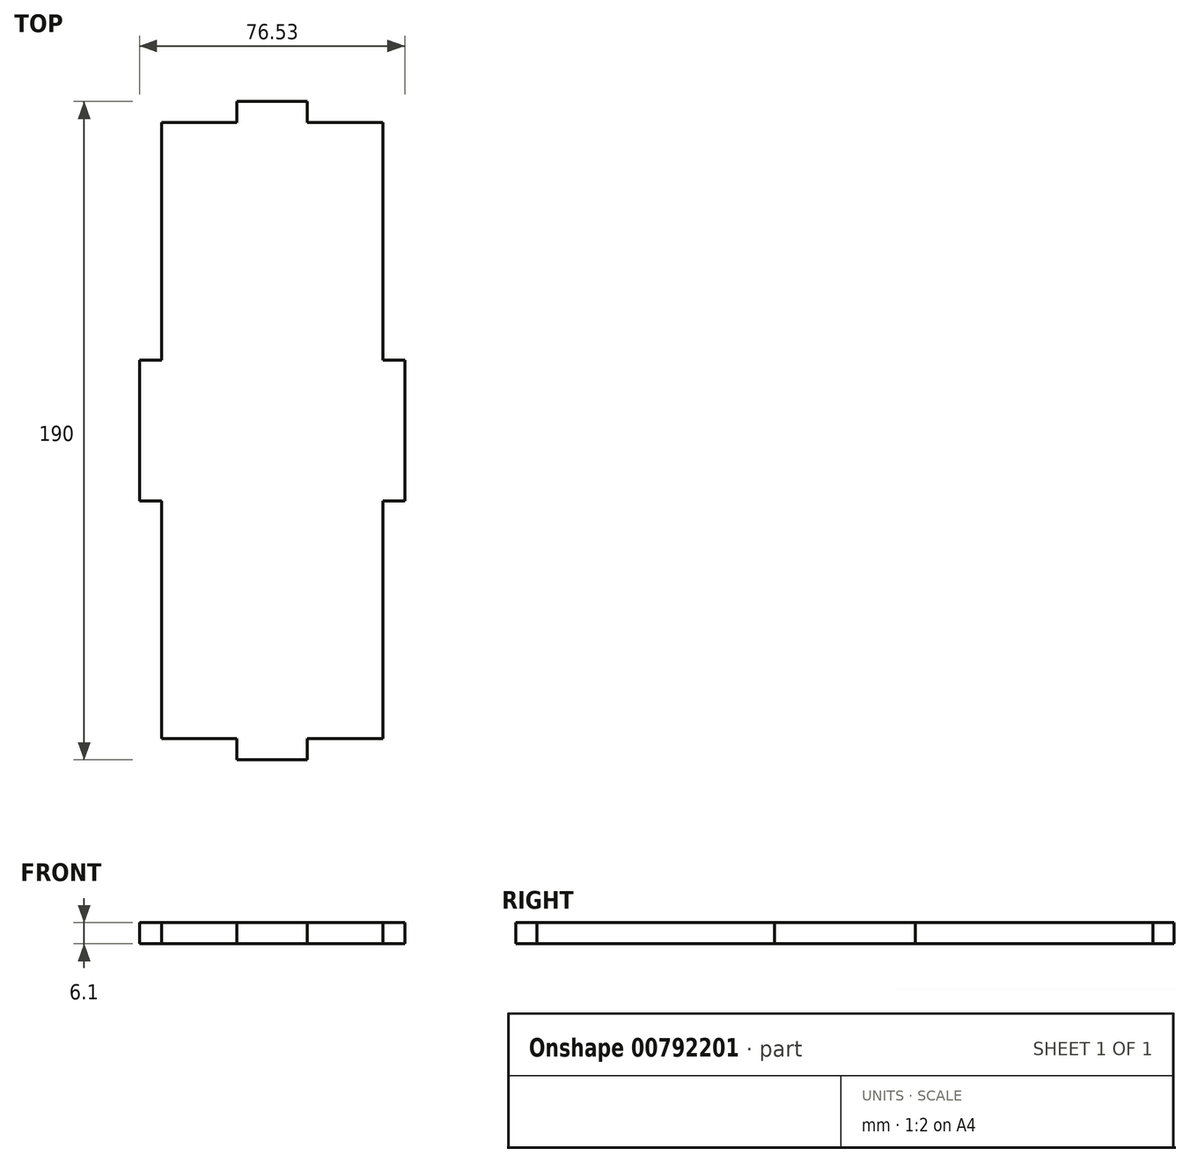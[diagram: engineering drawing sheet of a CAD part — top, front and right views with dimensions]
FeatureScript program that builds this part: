
annotation { "Feature Type Name" : "Feature", "Feature Type Description" : "" }
export const myFeature = defineFeature(function(context is Context, id is Id, definition is map)
    precondition{}
    {
        {
            var Q0;
            Q0=qCreatedBy(makeId("Top.planeOp"),FACE);
            var sketch = newSketch(context, id + "F0", { "sketchPlane" : qUnion([Q0])});
            skLineSegment(sketch, "E0.top", {"start": v(-37.7, 23.44) * mm, "end": v(-31.36, 23.44) * mm});
            skLineSegment(sketch, "E1.MirrorCS", {"start": v(-37.7, -17.2) * mm, "end": v(-31.36, -17.2) * mm});
            skLineSegment(sketch, "E2.MirrorCS", {"start": v(38.82, 23.44) * mm, "end": v(32.47, 23.44) * mm});
            skLineSegment(sketch, "E3.MirrorCS", {"start": v(38.82, -17.2) * mm, "end": v(32.47, -17.2) * mm});
            skLineSegment(sketch, "E4", {"start": v(-37.7, -17.2) * mm, "end": v(-37.7, 23.44) * mm});
            skLineSegment(sketch, "E5", {"start": v(38.82, -17.2) * mm, "end": v(38.82, 23.44) * mm});
            skLineSegment(sketch, "E6", {"start": v(-31.36, -17.2) * mm, "end": v(-31.36, -85.78) * mm});
            skLineSegment(sketch, "E7", {"start": v(32.47, -17.2) * mm, "end": v(32.47, -85.78) * mm});
            skLineSegment(sketch, "E8", {"start": v(-31.36, 23.44) * mm, "end": v(-31.36, 92.02) * mm});
            skLineSegment(sketch, "E9", {"start": v(32.47, 23.44) * mm, "end": v(32.47, 92.02) * mm});
            skLineSegment(sketch, "E10", {"start": v(-31.36, -85.78) * mm, "end": v(-9.6, -85.78) * mm});
            skLineSegment(sketch, "E11", {"start": v(32.47, 92.02) * mm, "end": v(10.71, 92.02) * mm});
            skLineSegment(sketch, "E12", {"start": v(32.47, -85.78) * mm, "end": v(10.71, -85.78) * mm});
            skLineSegment(sketch, "E13", {"start": v(10.71, -85.78) * mm, "end": v(10.71, -91.88) * mm});
            skLineSegment(sketch, "E14", {"start": v(10.71, -91.88) * mm, "end": v(-9.6, -91.88) * mm});
            skLineSegment(sketch, "E15", {"start": v(-9.6, -91.88) * mm, "end": v(-9.6, -85.78) * mm});
            skPoint(sketch, "E16.orphan", {"position": v(0.55, -85.78) * mm});
            skLineSegment(sketch, "E17.MirrorCS", {"start": v(-9.6, 98.12) * mm, "end": v(-9.6, 92.02) * mm});
            skLineSegment(sketch, "E18.MirrorCS", {"start": v(10.71, 98.12) * mm, "end": v(-9.6, 98.12) * mm});
            skLineSegment(sketch, "E19.MirrorCS", {"start": v(10.71, 92.02) * mm, "end": v(10.71, 98.12) * mm});
            skPoint(sketch, "E20.end.orphan", {"position": v(38.82, 3.12) * mm});
            skPoint(sketch, "E20.start.orphan", {"position": v(-37.7, 3.12) * mm});
            skLineSegment(sketch, "E21.trimOffspring", {"start": v(-9.6, 92.02) * mm, "end": v(-31.36, 92.02) * mm});
            skSolve(sketch);
        }
        {
            var Q0;
            Q0=makeQuery(id+"F0.imprint","IMPRINT",FACE,{"disambiguationData":[TD([[makeQuery(id+"F0.imprint","IMPRINT",EDGE,{"derivedFrom":sQuery(id+"F0.wireOp",EDGE,"E0.top")}),-1.0]])]});
            extrude(context, id + "F1", {"entities" : qUnion([Q0]), "depth" : 6.1 * mm, "offsetDistance" : 25.4 * mm});
        }
    });
